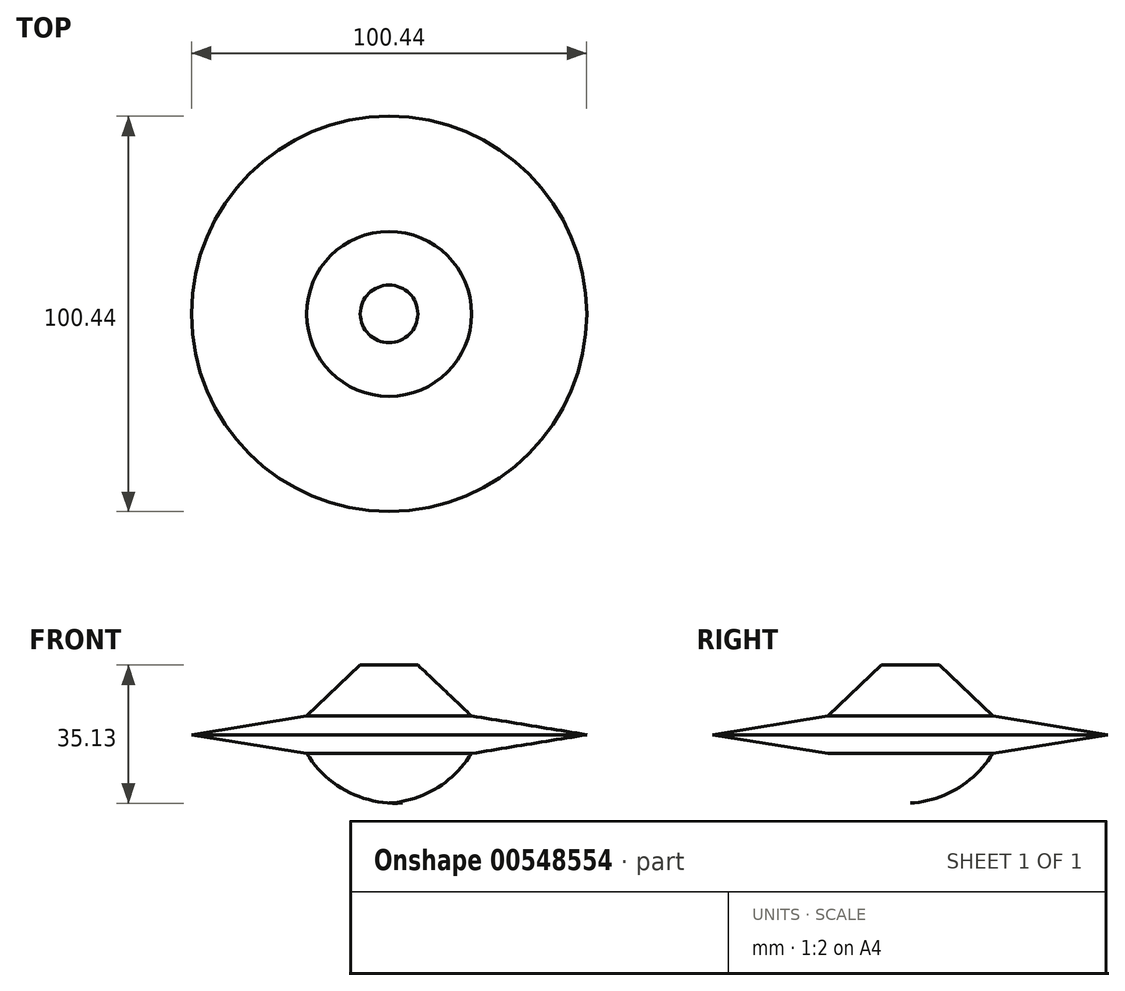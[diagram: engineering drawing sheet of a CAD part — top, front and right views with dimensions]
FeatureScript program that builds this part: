
annotation { "Feature Type Name" : "Feature", "Feature Type Description" : "" }
export const myFeature = defineFeature(function(context is Context, id is Id, definition is map)
    precondition{}
    {
        {
            var Q0;
            Q0=qCreatedBy(makeId("Front.planeOp"),FACE);
            var sketch = newSketch(context, id + "F0", { "sketchPlane" : qUnion([Q0])});
            skLineSegment(sketch, "E0", {"start": v(0, 35.07) * mm, "end": v(7.32, 35.07) * mm});
            skLineSegment(sketch, "E1", {"start": v(7.32, 35.07) * mm, "end": v(20.94, 22.13) * mm});
            skLineSegment(sketch, "E2", {"start": v(20.94, 22.13) * mm, "end": v(50.22, 17.37) * mm});
            skLineSegment(sketch, "E3", {"start": v(50.22, 17.37) * mm, "end": v(20.94, 12.6) * mm});
            skArc(sketch, "E4", {"start": v(0, 0) * mm, "mid": v(12, 3.75) * mm, "end": v(20.94, 12.6) * mm});
            skLineSegment(sketch, "E5", {"start": v(0, 35.07) * mm, "end": v(0, 0) * mm});
            skSolve(sketch);
        }
        {
            var Q0;
            Q0=makeQuery(id+"F0.imprint","IMPRINT",FACE,{"disambiguationData":[TD([[makeQuery(id+"F0.imprint","IMPRINT",EDGE,{"derivedFrom":sQuery(id+"F0.wireOp",EDGE,"E0")}),-1.0]])]});
            var Q1;
            Q1=sQuery(id+"F0.wireOp",EDGE,"E5");
            revolve(context, id + "F1", {"entities" : qUnion([Q0]), "axis" : qUnion([Q1]), "revolveType" : RevolveType.FULL});
        }
    });
